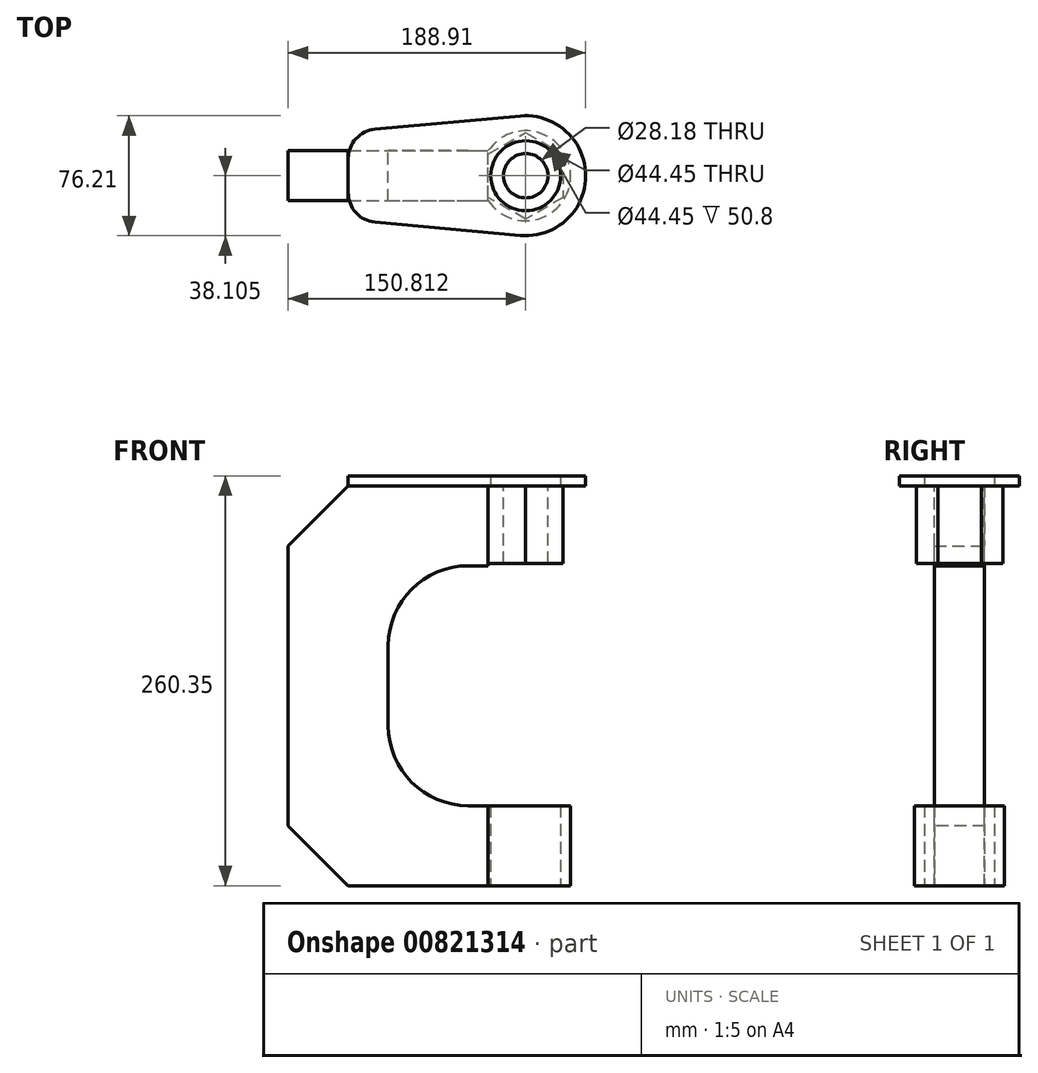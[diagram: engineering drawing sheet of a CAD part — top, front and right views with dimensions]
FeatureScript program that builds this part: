
annotation { "Feature Type Name" : "Feature", "Feature Type Description" : "" }
export const myFeature = defineFeature(function(context is Context, id is Id, definition is map)
    precondition{}
    {
        {
            var Q0;
            Q0=qCreatedBy(makeId("Front.planeOp"),FACE);
            var sketch = newSketch(context, id + "F0", { "sketchPlane" : qUnion([Q0])});
            skLineSegment(sketch, "E0.bottom", {"start": v(0, 0) * mm, "end": v(127, 0) * mm});
            skLineSegment(sketch, "E0.top", {"start": v(0, 254) * mm, "end": v(127, 254) * mm});
            skLineSegment(sketch, "E0.left", {"start": v(0, 0) * mm, "end": v(0, 254) * mm});
            skLineSegment(sketch, "E0.right", {"start": v(127, 0) * mm, "end": v(127, 50.8) * mm});
            skLineSegment(sketch, "E1", {"start": v(127, 203.2) * mm, "end": v(63.5, 203.2) * mm});
            skLineSegment(sketch, "E2", {"start": v(63.5, 203.2) * mm, "end": v(63.5, 50.8) * mm});
            skLineSegment(sketch, "E3", {"start": v(63.5, 50.8) * mm, "end": v(127, 50.8) * mm});
            skLineSegment(sketch, "E4.trimOffspring", {"start": v(127, 203.2) * mm, "end": v(127, 254) * mm});
            skSolve(sketch);
        }
        {
            var Q0;
            Q0=makeQuery(id+"F0.imprint","IMPRINT",FACE,{"disambiguationData":[TD([[makeQuery(id+"F0.imprint","IMPRINT",EDGE,{"derivedFrom":sQuery(id+"F0.wireOp",EDGE,"E0.bottom")}),1.0]])]});
            extrude(context, id + "F1", {"entities" : qUnion([Q0]), "depth" : 31.75 * mm, "offsetDistance" : 25.4 * mm});
        }
        {
            var Q0;
            Q0=makeQuery(id+"F1.opExtrude","SWEPT_EDGE",EDGE,{"disambiguationData":[OSD([sQuery(id+"F0.wireOp",EDGE,"E0.top"),sQuery(id+"F0.wireOp",EDGE,"E0.left")])]});
            var Q1;
            Q1=makeQuery(id+"F1.opExtrude","SWEPT_EDGE",EDGE,{"disambiguationData":[OSD([sQuery(id+"F0.wireOp",EDGE,"E0.bottom"),sQuery(id+"F0.wireOp",EDGE,"E0.left")])]});
            chamfer(context, id + "F2", {"entities" : qUnion([Q0, Q1]), "width" : 38.1 * mm, "tangentPropagation" : true});
        }
        {
            var Q0;
            Q0=makeQuery(id+"F1.opExtrude","SWEPT_EDGE",EDGE,{"disambiguationData":[OSD([sQuery(id+"F0.wireOp",EDGE,"E1"),sQuery(id+"F0.wireOp",EDGE,"E2")])]});
            var Q1;
            Q1=makeQuery(id+"F1.opExtrude","SWEPT_EDGE",EDGE,{"disambiguationData":[OSD([sQuery(id+"F0.wireOp",EDGE,"E2"),sQuery(id+"F0.wireOp",EDGE,"E3")])]});
            fillet(context, id + "F3", {"entities" : qUnion([Q0, Q1]), "radius" : 50.8 * mm, "tangentPropagation" : true, "allowEdgeOverflow" : false});
        }
        {
            var Q0;
            Q0=makeQuery(id+"F1.opExtrude","SWEPT_FACE",FACE,{"disambiguationData":[OSD([sQuery(id+"F0.wireOp",EDGE,"E0.top")])]});
            var sketch = newSketch(context, id + "F4", { "sketchPlane" : qUnion([Q0])});
            skCircle(sketch, "E5.cCircle", {"center": v(150.81, -15.88) * mm, "radius": 23.81 * mm, "construction": true});
            skLineSegment(sketch, "E5.0", {"start": v(150.81, -43.37) * mm, "end": v(127, -29.62) * mm});
            skLineSegment(sketch, "E5.1", {"start": v(127, -29.62) * mm, "end": v(127, -2.13) * mm});
            skLineSegment(sketch, "E5.2", {"start": v(127, -2.13) * mm, "end": v(150.81, 11.62) * mm});
            skLineSegment(sketch, "E5.3", {"start": v(150.81, 11.62) * mm, "end": v(174.62, -2.13) * mm});
            skLineSegment(sketch, "E5.4", {"start": v(174.62, -2.13) * mm, "end": v(174.62, -29.62) * mm});
            skLineSegment(sketch, "E5.5", {"start": v(174.62, -29.62) * mm, "end": v(150.81, -43.37) * mm});
            skPoint(sketch, "E5.0.midPoint", {"position": v(138.9, -36.5) * mm});
            skLineSegment(sketch, "E6", {"start": v(127, -15.88) * mm, "end": v(187.28, -15.88) * mm, "construction": true});
            skSolve(sketch);
        }
        {
            var Q0;
            Q0=makeQuery(id+"F4.imprint","IMPRINT",FACE,{"disambiguationData":[TD([[makeQuery(id+"F4.imprint","IMPRINT",EDGE,{"derivedFrom":sQuery(id+"F4.wireOp",EDGE,"E5.0")}),-1.0]])]});
            extrude(context, id + "F5", {"entities" : qUnion([Q0]), "oppositeDirection" : true, "depth" : 49.28 * mm, "offsetDistance" : 25.4 * mm});
        }
        {
            var Q0;
            Q0=makeQuery(id+"F5.opExtrude","CAP_FACE",FACE,{"disambiguationData":[OSD([sQuery(id+"F4.wireOp",EDGE,"E5.0"),sQuery(id+"F4.wireOp",EDGE,"E5.1"),sQuery(id+"F4.wireOp",EDGE,"E5.2"),sQuery(id+"F4.wireOp",EDGE,"E5.3"),sQuery(id+"F4.wireOp",EDGE,"E5.4"),sQuery(id+"F4.wireOp",EDGE,"E5.5")])],"isStart":true});
            var sketch = newSketch(context, id + "F6", { "sketchPlane" : qUnion([Q0])});
            skLineSegment(sketch, "E7", {"start": v(174.62, -15.87) * mm, "end": v(127, -15.88) * mm, "construction": true});
            skLineSegment(sketch, "E8", {"start": v(138.9, 4.75) * mm, "end": v(162.72, -36.5) * mm, "construction": true});
            skPoint(sketch, "E9", {"position": v(150.81, -15.88) * mm});
            skSolve(sketch);
        }
        {
            var Q0;
            Q0=sQuery(id+"F6.wireOp",VERTEX,"E9");
            var Q1;
            Q1=makeQuery(id+"F5.opExtrude","SWEPT_BODY",BODY,{"disambiguationData":[OSD([sQuery(id+"F4.wireOp",EDGE,"E5.0"),sQuery(id+"F4.wireOp",EDGE,"E5.1"),sQuery(id+"F4.wireOp",EDGE,"E5.2"),sQuery(id+"F4.wireOp",EDGE,"E5.3"),sQuery(id+"F4.wireOp",EDGE,"E5.4"),sQuery(id+"F4.wireOp",EDGE,"E5.5")])]});
            hole(context, id + "F7", {"style" : HoleStyle.SIMPLE, "endStyle" : HoleEndStyle.THROUGH, "standardTappedOrClearance" : lookupTablePath({ "standard" : "ANSI", "engagement" : "75%", "pitch" : "7 tpi", "size" : "1 1/4", "type" : "Tapped" }), "standardBlindInLast" : lookupTablePath({ "standard" : "ANSI", "engagement" : "75%", "pitch" : "7 tpi", "size" : "1 1/4", "type" : "Tapped" }), "holeDiameter" : 28.18 * mm, "majorDiameter" : 31.75 * mm, "showTappedDepth" : true, "isTappedThrough" : true, "tappedDepth" : 12.7 * mm, "tapClearance" : 3, "locations" : qUnion([Q0]), "scope" : qUnion([Q1])});
        }
        {
            var Q0;
            Q0=makeQuery(id+"F1.opExtrude","SWEPT_FACE",FACE,{"disambiguationData":[OSD([sQuery(id+"F0.wireOp",EDGE,"E0.bottom")])]});
            var sketch = newSketch(context, id + "F8", { "sketchPlane" : qUnion([Q0])});
            skCircle(sketch, "E10", {"center": v(150.81, 15.88) * mm, "radius": 28.58 * mm});
            skCircle(sketch, "E11", {"center": v(150.81, 15.88) * mm, "radius": 22.23 * mm});
            skSolve(sketch);
        }
        {
            var Q0;
            Q0=makeQuery(id+"F8.imprint","IMPRINT",FACE,{"disambiguationData":[TD([[makeQuery(id+"F8.imprint","IMPRINT",EDGE,{"derivedFrom":sQuery(id+"F8.wireOp",EDGE,"E11")}),-1.0]])]});
            extrude(context, id + "F9", {"entities" : qUnion([Q0]), "oppositeDirection" : true, "depth" : 50.8 * mm, "offsetDistance" : 25.4 * mm});
        }
        {
            var Q0;
            Q0=makeQuery(id+"F1.opExtrude","SWEPT_FACE",FACE,{"disambiguationData":[OSD([sQuery(id+"F0.wireOp",EDGE,"E0.top")])]});
            var sketch = newSketch(context, id + "F10", { "sketchPlane" : qUnion([Q0])});
            skArc(sketch, "E12", {"start": v(147.34, -53.82) * mm, "mid": v(188.91, -15.88) * mm, "end": v(147.34, 22.07) * mm});
            skLineSegment(sketch, "E13", {"start": v(38.1, -15.88) * mm, "end": v(112.71, -15.88) * mm, "construction": true});
            skLineSegment(sketch, "E14", {"start": v(38.1, -15.88) * mm, "end": v(38.1, 12.08) * mm});
            skLineSegment(sketch, "E15", {"start": v(38.1, 12.08) * mm, "end": v(147.34, 22.07) * mm});
            skLineSegment(sketch, "E16.MirrorCS", {"start": v(38.1, -43.83) * mm, "end": v(147.34, -53.82) * mm});
            skLineSegment(sketch, "E17.MirrorCS", {"start": v(38.1, -15.88) * mm, "end": v(38.1, -43.83) * mm});
            skCircle(sketch, "E18", {"center": v(150.81, -15.88) * mm, "radius": 22.23 * mm});
            skSolve(sketch);
        }
        {
            var Q0;
            Q0=makeQuery(id+"F10.imprint","IMPRINT",FACE,{"disambiguationData":[TD([[makeQuery(id+"F10.imprint","IMPRINT",EDGE,{"derivedFrom":sQuery(id+"F10.wireOp",EDGE,"E12")}),1.0]])]});
            var Q1;
            {var subQ0=sQuery(id+"F0.wireOp",EDGE,"E0.top");var subQ1=makeQuery(id+"F1.opExtrude","CAP_EDGE",EDGE,{"disambiguationData":[OSD([subQ0])],"isStart":true});Q1=makeQuery(id+"F10.imprint","IMPRINT",FACE,{"disambiguationData":[TD([[makeQuery(id+"F10.imprint","IMPRINT",EDGE,{"derivedFrom":subQ1}),-1.0]])]});}
            extrude(context, id + "F11", {"entities" : qUnion([Q0, Q1]), "depth" : 6.35 * mm, "offsetDistance" : 25.4 * mm});
        }
        {
            var Q0;
            Q0=makeQuery(id+"F11.opExtrude","SWEPT_EDGE",EDGE,{"disambiguationData":[OSD([sQuery(id+"F10.wireOp",EDGE,"E16.MirrorCS"),sQuery(id+"F10.wireOp",EDGE,"E17.MirrorCS")])]});
            var Q1;
            Q1=makeQuery(id+"F11.opExtrude","SWEPT_EDGE",EDGE,{"disambiguationData":[OSD([sQuery(id+"F10.wireOp",EDGE,"E14"),sQuery(id+"F10.wireOp",EDGE,"E15")])]});
            fillet(context, id + "F12", {"entities" : qUnion([Q0, Q1]), "radius" : 18.66 * mm, "tangentPropagation" : true, "allowEdgeOverflow" : false});
        }
    });
